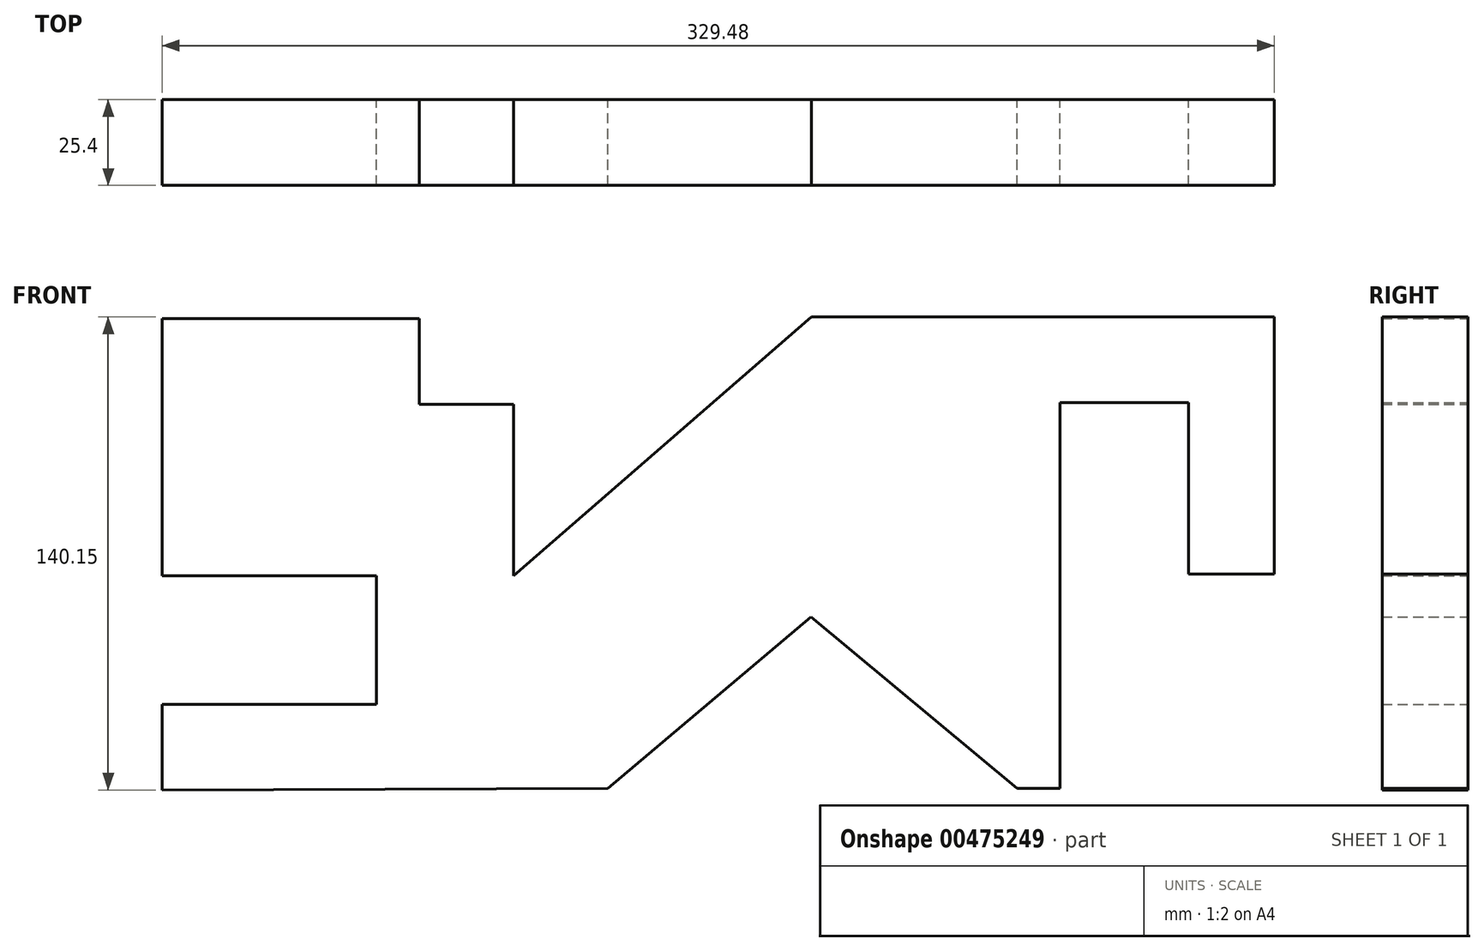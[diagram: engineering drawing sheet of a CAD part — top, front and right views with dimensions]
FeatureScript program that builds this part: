
annotation { "Feature Type Name" : "Feature", "Feature Type Description" : "" }
export const myFeature = defineFeature(function(context is Context, id is Id, definition is map)
    precondition{}
    {
        {
            var Q0;
            Q0=qCreatedBy(makeId("Front.planeOp"),FACE);
            var sketch = newSketch(context, id + "F0", { "sketchPlane" : qUnion([Q0])});
            skLineSegment(sketch, "E0", {"start": v(0, 0) * mm, "end": v(76.2, 0) * mm});
            skLineSegment(sketch, "E1", {"start": v(76.2, 0) * mm, "end": v(76.2, -25.4) * mm});
            skLineSegment(sketch, "E2", {"start": v(76.2, -25.4) * mm, "end": v(104.14, -25.4) * mm});
            skLineSegment(sketch, "E3", {"start": v(104.14, -25.4) * mm, "end": v(104.14, -76.2) * mm});
            skLineSegment(sketch, "E4", {"start": v(104.14, -76.2) * mm, "end": v(192.32, 0.45) * mm});
            skLineSegment(sketch, "E5", {"start": v(192.32, 0.45) * mm, "end": v(329.48, 0.45) * mm});
            skLineSegment(sketch, "E6", {"start": v(329.48, 0.45) * mm, "end": v(329.48, -75.75) * mm});
            skLineSegment(sketch, "E7", {"start": v(329.48, -75.75) * mm, "end": v(304.08, -75.75) * mm});
            skLineSegment(sketch, "E8", {"start": v(304.08, -75.75) * mm, "end": v(304.08, -24.95) * mm});
            skLineSegment(sketch, "E9", {"start": v(304.08, -24.95) * mm, "end": v(265.98, -24.95) * mm});
            skLineSegment(sketch, "E10", {"start": v(265.98, -24.95) * mm, "end": v(265.98, -139.25) * mm});
            skLineSegment(sketch, "E11", {"start": v(265.98, -139.25) * mm, "end": v(253.28, -139.25) * mm});
            skLineSegment(sketch, "E12", {"start": v(253.28, -139.25) * mm, "end": v(192.26, -88.4) * mm});
            skLineSegment(sketch, "E13", {"start": v(192.26, -88.4) * mm, "end": v(132.08, -139.25) * mm});
            skPoint(sketch, "E13.endSnap0", {"position": v(259.63, -139.25) * mm});
            skLineSegment(sketch, "E14", {"start": v(0, 0) * mm, "end": v(0, -76.2) * mm});
            skLineSegment(sketch, "E15", {"start": v(0, -76.2) * mm, "end": v(63.5, -76.2) * mm});
            skLineSegment(sketch, "E16", {"start": v(63.5, -76.2) * mm, "end": v(63.5, -114.3) * mm});
            skLineSegment(sketch, "E17", {"start": v(63.5, -114.3) * mm, "end": v(0, -114.3) * mm});
            skLineSegment(sketch, "E18", {"start": v(0, -114.3) * mm, "end": v(0, -139.7) * mm});
            skLineSegment(sketch, "E19", {"start": v(0, -139.7) * mm, "end": v(132.08, -139.25) * mm});
            skSolve(sketch);
        }
        {
            var Q0;
            Q0=makeQuery(id+"F0.imprint","IMPRINT",FACE,{"disambiguationData":[TD([[makeQuery(id+"F0.imprint","IMPRINT",EDGE,{"derivedFrom":sQuery(id+"F0.wireOp",EDGE,"E0")}),-1.0]])]});
            extrude(context, id + "F1", {"entities" : qUnion([Q0]), "depth" : 25.4 * mm});
        }
    });
